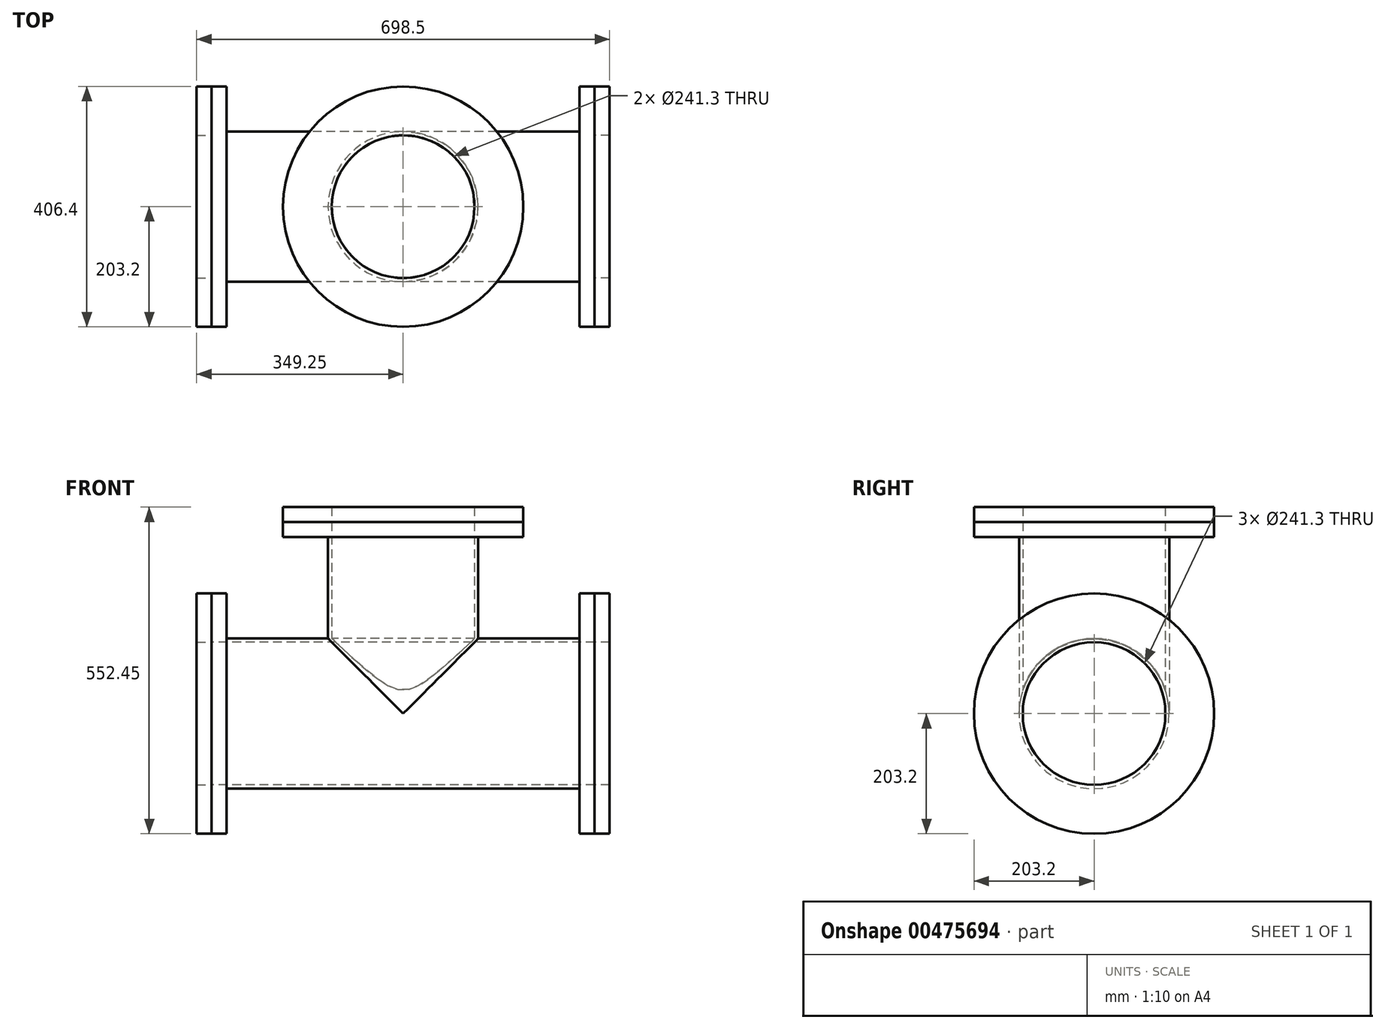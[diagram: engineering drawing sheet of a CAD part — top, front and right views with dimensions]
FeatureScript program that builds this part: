
annotation { "Feature Type Name" : "Feature", "Feature Type Description" : "" }
export const myFeature = defineFeature(function(context is Context, id is Id, definition is map)
    precondition{}
    {
        {
            var Q0;
            Q0=qCreatedBy(makeId("Top.planeOp"),FACE);
            var sketch = newSketch(context, id + "F0", { "sketchPlane" : qUnion([Q0])});
            skCircle(sketch, "E0", {"center": v(0, 0) * mm, "radius": 120.65 * mm});
            skCircle(sketch, "E1", {"center": v(0, 0) * mm, "radius": 127 * mm});
            skSolve(sketch);
        }
        {
            var Q0;
            Q0=makeQuery(id+"F0.imprint","IMPRINT",FACE,{"disambiguationData":[TD([[makeQuery(id+"F0.imprint","IMPRINT",EDGE,{"derivedFrom":sQuery(id+"F0.wireOp",EDGE,"E0")}),-1.0]])]});
            extrude(context, id + "F1", {"entities" : qUnion([Q0]), "depth" : 19.05 * mm});
        }
        {
            var Q0;
            Q0=makeQuery(id+"F1.opExtrude","CAP_FACE",FACE,{"disambiguationData":[OSD([sQuery(id+"F0.wireOp",EDGE,"E0"),sQuery(id+"F0.wireOp",EDGE,"E1")])],"isStart":false});
            var sketch = newSketch(context, id + "F2", { "sketchPlane" : qUnion([Q0])});
            skCircle(sketch, "E2", {"center": v(0, 0) * mm, "radius": 203.2 * mm});
            skSolve(sketch);
        }
        {
            var Q0;
            Q0=makeQuery(id+"F2.imprint","IMPRINT",FACE,{"disambiguationData":[TD([[makeQuery(id+"F2.imprint","IMPRINT",EDGE,{"derivedFrom":sQuery(id+"F2.wireOp",EDGE,"E2")}),1.0]])]});
            var Q1;
            Q1=makeQuery(id+"F2.imprint","IMPRINT",FACE,{"disambiguationData":[TD([[makeQuery(id+"F2.imprint","IMPRINT",EDGE,{"derivedFrom":makeQuery(id+"F1.opExtrude","CAP_EDGE",EDGE,{"disambiguationData":[OSD([sQuery(id+"F0.wireOp",EDGE,"E0")])],"isStart":false})}),-1.0]])]});
            extrude(context, id + "F3", {"entities" : qUnion([Q0, Q1]), "operationType" : NewBodyOperationType.ADD, "depth" : 25.4 * mm});
        }
        {
            var Q0;
            Q0=qCreatedBy(makeId("Front.planeOp"),FACE);
            var sketch = newSketch(context, id + "F4", { "sketchPlane" : qUnion([Q0])});
            skLineSegment(sketch, "E3", {"start": v(0, 0) * mm, "end": v(0, -127) * mm, "construction": true});
            skLineSegment(sketch, "E4", {"start": v(-152.4, -279.4) * mm, "end": v(-279.4, -279.4) * mm, "construction": true});
            skPoint(sketch, "E5.visualSharp", {"position": v(0, -279.4) * mm});
            skArc(sketch, "E5.filletArc", {"start": v(-152.4, -279.4) * mm, "mid": v(-44.64, -234.76) * mm, "end": v(0, -127) * mm, "construction": true});
            skArc(sketch, "E6.MirrorCS", {"start": v(152.4, -279.4) * mm, "mid": v(44.64, -234.76) * mm, "end": v(0, -127) * mm, "construction": true});
            skLineSegment(sketch, "E7.MirrorCS", {"start": v(152.4, -279.4) * mm, "end": v(279.4, -279.4) * mm, "construction": true});
            skSolve(sketch);
        }
        {
            var Q0;
            Q0=qCreatedBy(makeId("Front.planeOp"),FACE);
            var sketch = newSketch(context, id + "F5", { "sketchPlane" : qUnion([Q0])});
            skLineSegment(sketch, "E8", {"start": v(0, 0) * mm, "end": v(0, -172.58) * mm, "construction": true});
            skSolve(sketch);
        }
        {
            var Q0;
            Q0=qCreatedBy(makeId("Right.planeOp"),FACE);
            var Q1;
            Q1=sQuery(id+"F4.wireOp",VERTEX,"E7.MirrorCS.end");
            cPlane(context, id + "F6", {"entities" : qUnion([Q0, Q1]), "cplaneType" : CPlaneType.PLANE_POINT, "offset" : 25.4 * mm, "width" : 152.4 * mm, "height" : 152.4 * mm});
        }
        {
            var Q0;
            Q0=makeQuery(id+"F1.opExtrude","SWEPT_BODY",BODY,{"disambiguationData":[OSD([sQuery(id+"F0.wireOp",EDGE,"E0"),sQuery(id+"F0.wireOp",EDGE,"E1")])]});
            var Q1;
            Q1=sQuery(id+"F5.wireOp",VERTEX,"E8.start");
            var Q2;
            Q2=sQuery(id+"F4.wireOp",VERTEX,"E7.MirrorCS.end");
            transform(context, id + "F7", {"entities" : qUnion([Q0]), "transformType" : TransformType.TRANSLATION_ENTITY, "oppositeDirectionEntity" : false, "transformLine" : qUnion([Q1, Q2]), "makeCopy" : true});
        }
        {
            var Q0;
            Q0=qCreatedBy(id+"F6.planeOp",FACE);
            var sketch = newSketch(context, id + "F8", { "sketchPlane" : qUnion([Q0])});
            skLineSegment(sketch, "E9", {"start": v(-1.27, -279.4) * mm, "end": v(245.65, -279.4) * mm, "construction": true});
            skSolve(sketch);
        }
        {
            var Q0;
            Q0=makeQuery(id+"F7.opPattern","COPY",BODY,{"derivedFrom":makeQuery(id+"F1.opExtrude","SWEPT_BODY",BODY,{"disambiguationData":[OSD([sQuery(id+"F0.wireOp",EDGE,"E0"),sQuery(id+"F0.wireOp",EDGE,"E1")])]}),"instanceName":"1"});
            var Q1;
            Q1=sQuery(id+"F8.wireOp",EDGE,"E9");
            transform(context, id + "F9", {"entities" : qUnion([Q0]), "transformType" : TransformType.ROTATION, "transformAxis" : qUnion([Q1]), "angle" : 90 * degree, "makeCopy" : false});
        }
        {
            var Q0;
            Q0=makeQuery(id+"F7.opPattern","COPY",BODY,{"derivedFrom":makeQuery(id+"F1.opExtrude","SWEPT_BODY",BODY,{"disambiguationData":[OSD([sQuery(id+"F0.wireOp",EDGE,"E0"),sQuery(id+"F0.wireOp",EDGE,"E1")])]}),"instanceName":"1"});
            var Q1;
            Q1=qCreatedBy(makeId("Right.planeOp"),FACE);
            mirror(context, id + "F10", {"entities" : qUnion([Q0]), "mirrorPlane" : qUnion([Q1])});
        }
        {
            var Q0;
            Q0=makeQuery(id+"F7.opPattern","COPY",FACE,{"derivedFrom":makeQuery(id+"F1.opExtrude","CAP_FACE",FACE,{"disambiguationData":[OSD([sQuery(id+"F0.wireOp",EDGE,"E0"),sQuery(id+"F0.wireOp",EDGE,"E1")])],"isStart":true}),"instanceName":"1"});
            var Q1;
            Q1=makeQuery(id+"F10.opPattern","COPY",FACE,{"derivedFrom":makeQuery(id+"F7.opPattern","COPY",FACE,{"derivedFrom":makeQuery(id+"F1.opExtrude","CAP_FACE",FACE,{"disambiguationData":[OSD([sQuery(id+"F0.wireOp",EDGE,"E0"),sQuery(id+"F0.wireOp",EDGE,"E1")])],"isStart":true}),"instanceName":"1"}),"instanceName":"1"});
            extrude(context, id + "F11", {"entities" : qUnion([Q0]), "operationType" : NewBodyOperationType.ADD, "endBound" : BoundingType.UP_TO_SURFACE, "endBoundEntityFace" : qUnion([Q1]), "depth" : 25.4 * mm});
        }
        {
            var Q0;
            Q0=makeQuery(id+"F0.imprint","IMPRINT",FACE,{"disambiguationData":[TD([[makeQuery(id+"F0.imprint","IMPRINT",EDGE,{"derivedFrom":sQuery(id+"F0.wireOp",EDGE,"E0")}),-1.0]])]});
            var Q1;
            {var subQ0=sQuery(id+"F0.wireOp",EDGE,"E1");var subQ1=makeQuery(id+"F7.opPattern","COPY",FACE,{"derivedFrom":makeQuery(id+"F1.opExtrude","SWEPT_FACE",FACE,{"disambiguationData":[OSD([subQ0])]}),"instanceName":"1"});Q1=makeQuery(id+"F11.boolean.opBoolean","MERGE",FACE,{"derivedFrom":[subQ1,makeQuery(id+"F10.opPattern","COPY",FACE,{"derivedFrom":subQ1,"instanceName":"1"}),makeQuery(id+"F11.opExtrude","SWEPT_FACE",FACE,{"disambiguationData":[OSD([subQ0])]})]});}
            extrude(context, id + "F12", {"entities" : qUnion([Q0]), "operationType" : NewBodyOperationType.ADD, "endBound" : BoundingType.UP_TO_SURFACE, "oppositeDirection" : true, "endBoundEntityFace" : qUnion([Q1]), "depth" : 25.4 * mm});
        }
        {
            var Q0;
            Q0=makeQuery(id+"F7.opPattern","COPY",FACE,{"derivedFrom":makeQuery(id+"F3.opExtrude","CAP_FACE",FACE,{"disambiguationData":[OSD([sQuery(id+"F0.wireOp",EDGE,"E0"),sQuery(id+"F2.wireOp",EDGE,"E2")])],"isStart":false}),"instanceName":"1"});
            extrude(context, id + "F13", {"entities" : qUnion([Q0]), "depth" : 25.4 * mm});
        }
        {
            var Q0;
            Q0=makeQuery(id+"F10.opPattern","COPY",FACE,{"derivedFrom":makeQuery(id+"F7.opPattern","COPY",FACE,{"derivedFrom":makeQuery(id+"F3.opExtrude","CAP_FACE",FACE,{"disambiguationData":[OSD([sQuery(id+"F0.wireOp",EDGE,"E0"),sQuery(id+"F2.wireOp",EDGE,"E2")])],"isStart":false}),"instanceName":"1"}),"instanceName":"1"});
            extrude(context, id + "F14", {"entities" : qUnion([Q0]), "depth" : 25.4 * mm});
        }
        {
            var Q0;
            Q0=makeQuery(id+"F3.opExtrude","CAP_FACE",FACE,{"disambiguationData":[OSD([sQuery(id+"F0.wireOp",EDGE,"E0"),sQuery(id+"F2.wireOp",EDGE,"E2")])],"isStart":false});
            extrude(context, id + "F15", {"entities" : qUnion([Q0]), "depth" : 25.4 * mm});
        }
    });
